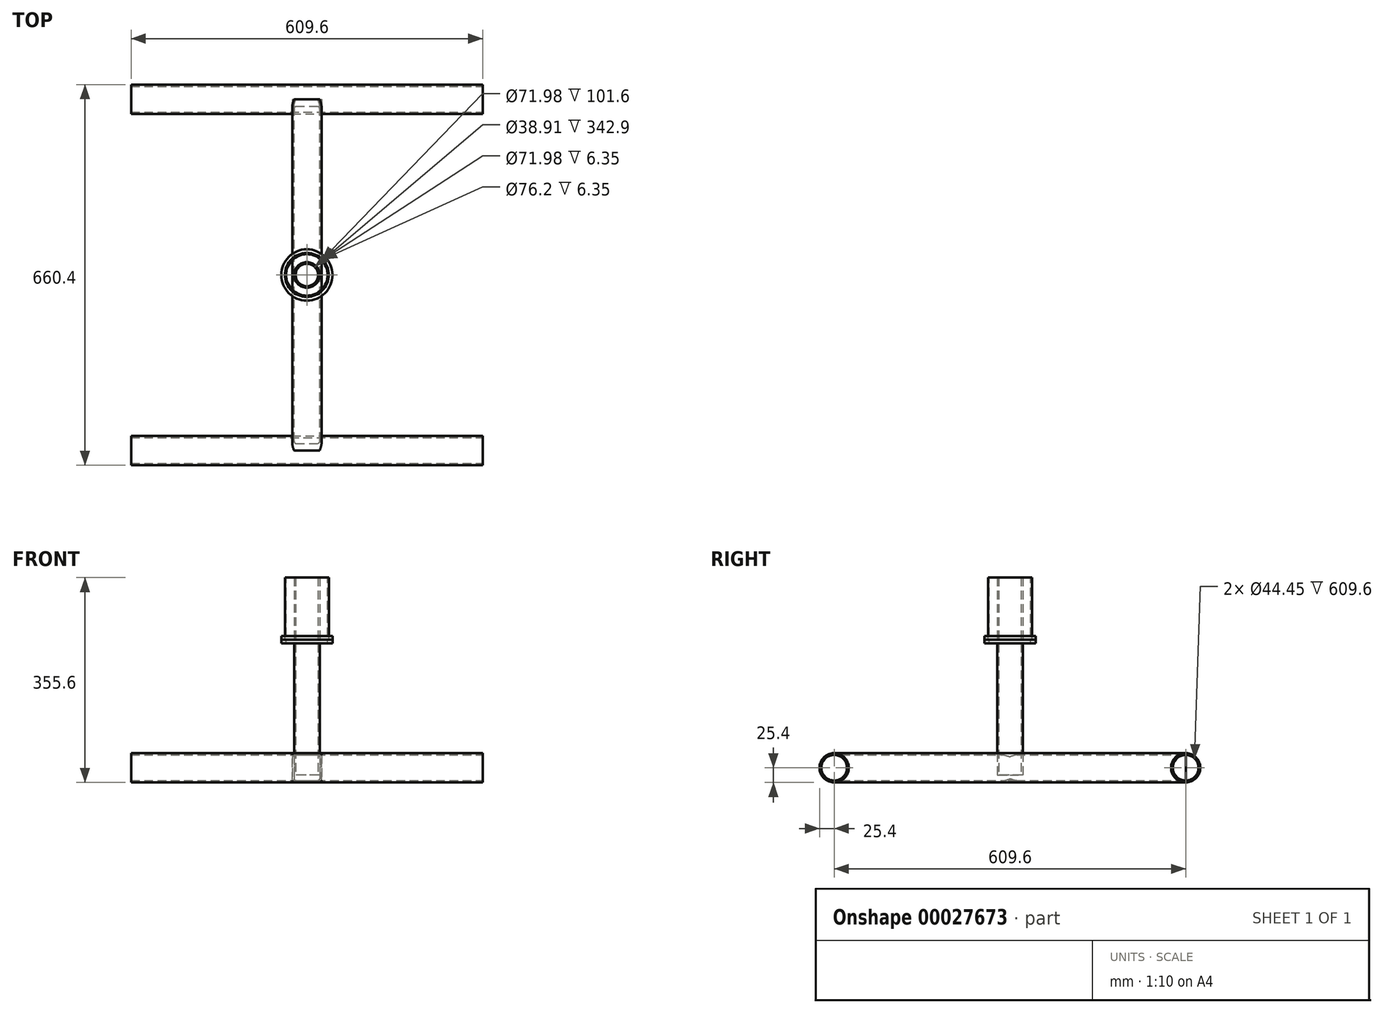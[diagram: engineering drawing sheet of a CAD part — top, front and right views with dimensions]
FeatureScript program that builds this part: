
annotation { "Feature Type Name" : "Feature", "Feature Type Description" : "" }
export const myFeature = defineFeature(function(context is Context, id is Id, definition is map)
    precondition{}
    {
        {
            var Q0;
            Q0=qCreatedBy(makeId("Front.planeOp"),FACE);
            var sketch = newSketch(context, id + "F0", { "sketchPlane" : qUnion([Q0])});
            skLineSegment(sketch, "E0.bottom", {"start": v(-19.05, 22.22) * mm, "end": v(19.05, 22.22) * mm});
            skLineSegment(sketch, "E0.top", {"start": v(-19.05, -22.23) * mm, "end": v(19.05, -22.23) * mm});
            skLineSegment(sketch, "E0.left", {"start": v(-22.23, 19.05) * mm, "end": v(-22.23, -19.05) * mm});
            skLineSegment(sketch, "E0.right", {"start": v(22.23, 19.05) * mm, "end": v(22.22, -19.05) * mm});
            skLineSegment(sketch, "E1", {"start": v(-22.23, 22.23) * mm, "end": v(22.23, -22.23) * mm, "construction": true});
            skLineSegment(sketch, "E2.0", {"start": v(25.4, 22.22) * mm, "end": v(25.4, -22.23) * mm});
            skLineSegment(sketch, "E2.1", {"start": v(-22.23, 25.4) * mm, "end": v(22.23, 25.4) * mm});
            skLineSegment(sketch, "E2.2", {"start": v(-25.4, 22.22) * mm, "end": v(-25.4, -22.23) * mm});
            skLineSegment(sketch, "E2.3", {"start": v(-22.23, -25.4) * mm, "end": v(22.22, -25.4) * mm});
            skPoint(sketch, "E3.visualSharp", {"position": v(-22.23, 22.22) * mm});
            skArc(sketch, "E3.filletArc", {"start": v(-19.05, 22.22) * mm, "mid": v(-21.3, 21.3) * mm, "end": v(-22.23, 19.05) * mm});
            skPoint(sketch, "E4.visualSharp", {"position": v(22.23, 22.22) * mm});
            skArc(sketch, "E4.filletArc", {"start": v(22.23, 19.05) * mm, "mid": v(21.3, 21.3) * mm, "end": v(19.05, 22.22) * mm});
            skPoint(sketch, "E5.visualSharp", {"position": v(22.22, -22.23) * mm});
            skArc(sketch, "E5.filletArc", {"start": v(19.05, -22.23) * mm, "mid": v(21.3, -21.3) * mm, "end": v(22.22, -19.05) * mm});
            skPoint(sketch, "E6.visualSharp", {"position": v(-22.23, -22.23) * mm});
            skArc(sketch, "E6.filletArc", {"start": v(-22.23, -19.05) * mm, "mid": v(-21.3, -21.3) * mm, "end": v(-19.05, -22.23) * mm});
            skPoint(sketch, "E7.visualSharp", {"position": v(-25.4, -25.4) * mm});
            skArc(sketch, "E7.filletArc", {"start": v(-25.4, -22.23) * mm, "mid": v(-24.47, -24.47) * mm, "end": v(-22.23, -25.4) * mm});
            skPoint(sketch, "E8.visualSharp", {"position": v(25.4, -25.4) * mm});
            skArc(sketch, "E8.filletArc", {"start": v(22.22, -25.4) * mm, "mid": v(24.47, -24.47) * mm, "end": v(25.4, -22.23) * mm});
            skPoint(sketch, "E9.visualSharp", {"position": v(25.4, 25.4) * mm});
            skArc(sketch, "E9.filletArc", {"start": v(25.4, 22.22) * mm, "mid": v(24.47, 24.47) * mm, "end": v(22.23, 25.4) * mm});
            skPoint(sketch, "E10.visualSharp", {"position": v(-25.4, 25.4) * mm});
            skArc(sketch, "E10.filletArc", {"start": v(-22.23, 25.4) * mm, "mid": v(-24.47, 24.47) * mm, "end": v(-25.4, 22.22) * mm});
            skSolve(sketch);
        }
        {
            var Q0;
            Q0 = qSketchRegion(id + "F0", true);
            extrude(context, id + "F1", {"entities" : qUnion([Q0]), "depth" : 304.8 * mm, "hasSecondDirection" : true, "secondDirectionOppositeDirection" : true, "secondDirectionDepth" : 304.8 * mm});
        }
        {
            var Q0;
            Q0=qCreatedBy(makeId("Right.planeOp"),FACE);
            var sketch = newSketch(context, id + "F2", { "sketchPlane" : qUnion([Q0])});
            skCircle(sketch, "E11", {"center": v(-304.8, 0) * mm, "radius": 25.4 * mm});
            skCircle(sketch, "E12.0", {"center": v(-304.8, 0) * mm, "radius": 22.23 * mm});
            skLineSegment(sketch, "E13", {"start": v(0, 0) * mm, "end": v(0, 100.46) * mm, "construction": true});
            skCircle(sketch, "E14.MirrorC", {"center": v(304.8, 0) * mm, "radius": 25.4 * mm});
            skCircle(sketch, "E15.MirrorC", {"center": v(304.8, 0) * mm, "radius": 22.23 * mm});
            skSolve(sketch);
        }
        {
            var Q0;
            Q0=makeQuery(id+"F2.imprint","IMPRINT",FACE,{"disambiguationData":[TD([[makeQuery(id+"F2.imprint","IMPRINT",EDGE,{"derivedFrom":sQuery(id+"F2.wireOp",EDGE,"E12.0")}),1.0]])]});
            var Q1;
            Q1=makeQuery(id+"F2.imprint","IMPRINT",FACE,{"disambiguationData":[TD([[makeQuery(id+"F2.imprint","IMPRINT",EDGE,{"derivedFrom":sQuery(id+"F2.wireOp",EDGE,"E11")}),1.0]])]});
            var Q2;
            Q2=makeQuery(id+"F2.imprint","IMPRINT",FACE,{"disambiguationData":[TD([[makeQuery(id+"F2.imprint","IMPRINT",EDGE,{"derivedFrom":sQuery(id+"F2.wireOp",EDGE,"E14.MirrorC")}),-1.0]])]});
            var Q3;
            Q3=makeQuery(id+"F2.imprint","IMPRINT",FACE,{"disambiguationData":[TD([[makeQuery(id+"F2.imprint","IMPRINT",EDGE,{"derivedFrom":sQuery(id+"F2.wireOp",EDGE,"E15.MirrorC")}),-1.0]])]});
            extrude(context, id + "F3", {"entities" : qUnion([Q0, Q1, Q2, Q3]), "operationType" : NewBodyOperationType.REMOVE, "endBound" : BoundingType.THROUGH_ALL, "oppositeDirection" : true, "depth" : 25.4 * mm, "hasSecondDirection" : true, "secondDirectionBound" : BoundingType.THROUGH_ALL, "secondDirectionOppositeDirection" : false, "secondDirectionDepth" : 25.4 * mm});
        }
        {
            var Q0;
            Q0=makeQuery(id+"F2.imprint","IMPRINT",FACE,{"disambiguationData":[TD([[makeQuery(id+"F2.imprint","IMPRINT",EDGE,{"derivedFrom":sQuery(id+"F2.wireOp",EDGE,"E11")}),1.0]])]});
            extrude(context, id + "F4", {"entities" : qUnion([Q0]), "oppositeDirection" : true, "depth" : 304.8 * mm, "hasSecondDirection" : true, "secondDirectionOppositeDirection" : false, "secondDirectionDepth" : 304.8 * mm});
        }
        {
            var Q0;
            Q0=makeQuery(id+"F4.opExtrude","SWEPT_BODY",BODY,{"disambiguationData":[OSD([sQuery(id+"F2.wireOp",EDGE,"E11"),sQuery(id+"F2.wireOp",EDGE,"E12.0")])]});
            var Q1;
            Q1=qCreatedBy(makeId("Front.planeOp"),FACE);
            mirror(context, id + "F5", {"entities" : qUnion([Q0]), "mirrorPlane" : qUnion([Q1])});
        }
        {
            var Q0;
            Q0=makeQuery(id+"F1.opExtrude","SWEPT_FACE",FACE,{"disambiguationData":[OSD([sQuery(id+"F0.wireOp",EDGE,"E2.1")])]});
            var sketch = newSketch(context, id + "F6", { "sketchPlane" : qUnion([Q0])});
            skCircle(sketch, "E16", {"center": v(0, 0) * mm, "radius": 22.23 * mm});
            skCircle(sketch, "E17.0", {"center": v(0, 0) * mm, "radius": 19.46 * mm});
            skSolve(sketch);
        }
        {
            var Q0;
            Q0=makeQuery(id+"F6.imprint","IMPRINT",FACE,{"disambiguationData":[TD([[makeQuery(id+"F6.imprint","IMPRINT",EDGE,{"derivedFrom":sQuery(id+"F6.wireOp",EDGE,"E17.0")}),1.0]])]});
            var Q1;
            Q1=makeQuery(id+"F6.imprint","IMPRINT",FACE,{"disambiguationData":[TD([[makeQuery(id+"F6.imprint","IMPRINT",EDGE,{"derivedFrom":sQuery(id+"F6.wireOp",EDGE,"E17.0")}),-1.0]])]});
            var Q2;
            Q2=makeQuery(id+"F1.opExtrude","SWEPT_FACE",FACE,{"disambiguationData":[OSD([sQuery(id+"F0.wireOp",EDGE,"E0.top")])]});
            extrude(context, id + "F7", {"entities" : qUnion([Q0, Q1]), "operationType" : NewBodyOperationType.REMOVE, "endBound" : BoundingType.UP_TO_SURFACE, "oppositeDirection" : true, "endBoundEntityFace" : qUnion([Q2]), "depth" : 25.4 * mm});
        }
        {
            var Q0;
            Q0 = qSketchRegion(id + "F6", true);
            extrude(context, id + "F8", {"entities" : qUnion([Q0]), "depth" : 304.8 * mm, "hasSecondDirection" : true, "secondDirectionOppositeDirection" : true, "secondDirectionDepth" : 38.1 * mm});
        }
        {
            var Q0;
            Q0=makeQuery(id+"F8.opExtrude","CAP_FACE",FACE,{"disambiguationData":[OSD([sQuery(id+"F6.wireOp",EDGE,"E16"),sQuery(id+"F6.wireOp",EDGE,"E17.0")])],"isStart":false});
            var sketch = newSketch(context, id + "F9", { "sketchPlane" : qUnion([Q0])});
            skCircle(sketch, "E18.0", {"center": v(0, 0) * mm, "radius": 36 * mm});
            skCircle(sketch, "E19.0", {"center": v(0, 0) * mm, "radius": 38.1 * mm});
            skSolve(sketch);
        }
        {
            var Q0;
            Q0 = qSketchRegion(id + "F9", true);
            extrude(context, id + "F10", {"entities" : qUnion([Q0]), "oppositeDirection" : true, "depth" : 101.6 * mm});
        }
        {
            var Q0;
            Q0=makeQuery(id+"F10.opExtrude","CAP_FACE",FACE,{"disambiguationData":[OSD([sQuery(id+"F9.wireOp",EDGE,"E18.0"),sQuery(id+"F9.wireOp",EDGE,"E19.0")])],"isStart":false});
            var sketch = newSketch(context, id + "F11", { "sketchPlane" : qUnion([Q0])});
            skSolve(sketch);
        }
        {
            var Q0;
            Q0=makeQuery(id+"F11.imprint","IMPRINT",FACE,{"disambiguationData":[TD([[makeQuery(id+"F11.imprint","IMPRINT",EDGE,{"derivedFrom":makeQuery(id+"F10.opExtrude","CAP_EDGE",EDGE,{"disambiguationData":[OSD([sQuery(id+"F9.wireOp",EDGE,"E18.0")])],"isStart":false})}),1.0]])]});
            var sketch = newSketch(context, id + "F12", { "sketchPlane" : qUnion([Q0])});
            skCircle(sketch, "E20", {"center": v(0, 0) * mm, "radius": 38.1 * mm});
            skCircle(sketch, "E21", {"center": v(0, 0) * mm, "radius": 44.45 * mm});
            skSolve(sketch);
        }
        {
            var Q0;
            Q0=makeQuery(id+"F12.imprint","IMPRINT",FACE,{"disambiguationData":[TD([[makeQuery(id+"F12.imprint","IMPRINT",EDGE,{"derivedFrom":sQuery(id+"F12.wireOp",EDGE,"E20")}),1.0]])]});
            extrude(context, id + "F13", {"entities" : qUnion([Q0]), "depth" : 6.35 * mm});
        }
        {
            var Q0;
            Q0=makeQuery(id+"F13.opExtrude","CAP_FACE",FACE,{"disambiguationData":[OSD([sQuery(id+"F12.wireOp",EDGE,"E20"),sQuery(id+"F12.wireOp",EDGE,"E21")])],"isStart":false});
            var sketch = newSketch(context, id + "F14", { "sketchPlane" : qUnion([Q0])});
            skCircle(sketch, "E22.0", {"center": v(0, 0) * mm, "radius": 44.45 * mm});
            skCircle(sketch, "E23", {"center": v(0, 0) * mm, "radius": 36 * mm});
            skSolve(sketch);
        }
        {
            var Q0;
            Q0 = qSketchRegion(id + "F14", true);
            extrude(context, id + "F15", {"entities" : qUnion([Q0]), "depth" : 6.35 * mm});
        }
    });
